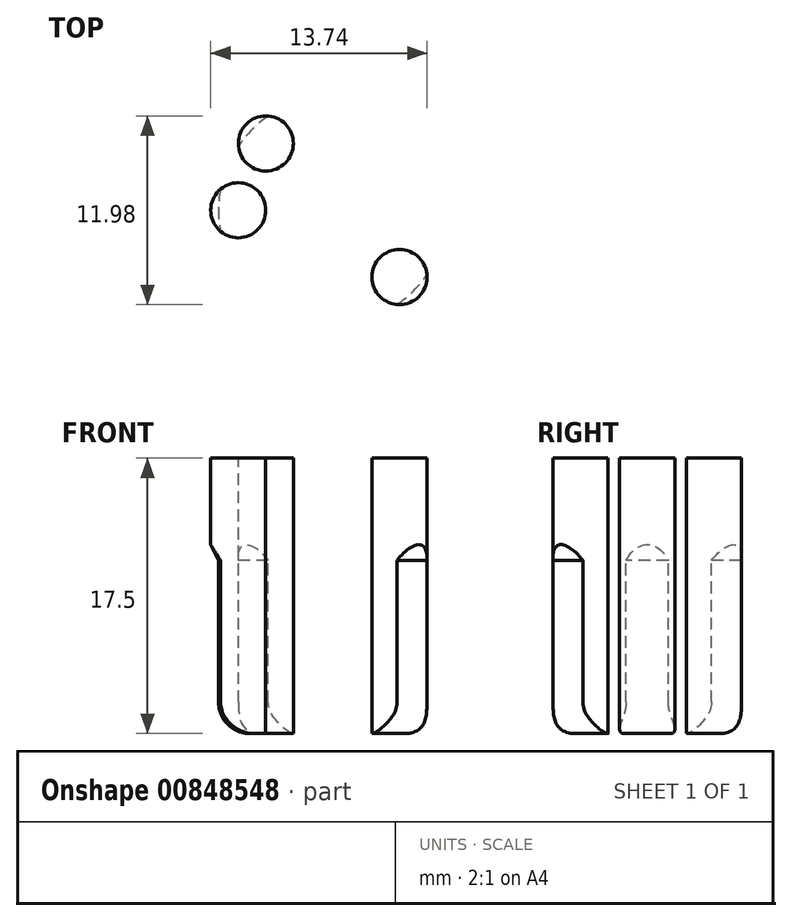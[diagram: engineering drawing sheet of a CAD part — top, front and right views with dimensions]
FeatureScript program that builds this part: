
annotation { "Feature Type Name" : "Feature", "Feature Type Description" : "" }
export const myFeature = defineFeature(function(context is Context, id is Id, definition is map)
    precondition{}
    {
        {
            var Q0;
            Q0=qCreatedBy(makeId("Top.planeOp"),FACE);
            var sketch = newSketch(context, id + "F0", { "sketchPlane" : qUnion([Q0])});
            skCircle(sketch, "E0", {"center": v(0, 0) * mm, "radius": 7.25 * mm});
            skSolve(sketch);
        }
        {
            var Q0;
            Q0 = qSketchRegion(id + "F0", true);
            extrude(context, id + "F1", {"entities" : qUnion([Q0]), "oppositeDirection" : true, "depth" : 10.5 * mm, "offsetDistance" : 25 * mm});
        }
        {
            var Q0;
            Q0=qCreatedBy(makeId("Top.planeOp"),FACE);
            var sketch = newSketch(context, id + "F2", { "sketchPlane" : qUnion([Q0])});
            skCircle(sketch, "E1", {"center": v(0, 0) * mm, "radius": 10 * mm});
            skSolve(sketch);
        }
        {
            var Q0;
            Q0 = qSketchRegion(id + "F2", true);
            extrude(context, id + "F3", {"entities" : qUnion([Q0]), "operationType" : NewBodyOperationType.ADD, "depth" : 7 * mm, "offsetDistance" : 25 * mm});
        }
        {
            var Q0;
            Q0=makeQuery(id+"F3.opExtrude","CAP_EDGE",EDGE,{"disambiguationData":[OSD([sQuery(id+"F2.wireOp",EDGE,"E1")])],"isStart":true});
            chamfer(context, id + "F4", {"entities" : qUnion([Q0]), "chamferType" : ChamferType.TWO_OFFSETS, "width1" : 6 * mm, "oppositeDirection" : false, "width2" : 3 * mm, "tangentPropagation" : true});
        }
        {
            var Q0;
            Q0=makeQuery(id+"F3.opExtrude","CAP_FACE",FACE,{"disambiguationData":[OSD([sQuery(id+"F2.wireOp",EDGE,"E1")])],"isStart":false});
            var sketch = newSketch(context, id + "F5", { "sketchPlane" : qUnion([Q0])});
            skCircle(sketch, "E2", {"center": v(0, 0) * mm, "radius": 2.75 * mm});
            skCircle(sketch, "E3", {"center": v(0, 6) * mm, "radius": 1.75 * mm});
            skLineSegment(sketch, "E4", {"start": v(0, 0) * mm, "end": v(7.93, 7.93) * mm, "construction": true});
            skCircle(sketch, "E5", {"center": v(4.24, 4.24) * mm, "radius": 1.75 * mm});
            skCircle(sketch, "E6.1.0", {"center": v(6, 0) * mm, "radius": 1.75 * mm});
            skCircle(sketch, "E6.2.0", {"center": v(0, -6) * mm, "radius": 1.75 * mm});
            skLineSegment(sketch, "E6.anchor1", {"start": v(0, 0) * mm, "end": v(0, 6) * mm, "construction": true});
            skLineSegment(sketch, "E6.anchor2", {"start": v(0, 0) * mm, "end": v(0, -6) * mm, "construction": true});
            skCircle(sketch, "E7.MirrorC", {"center": v(4.24, -4.24) * mm, "radius": 1.75 * mm});
            skCircle(sketch, "E8.MirrorC", {"center": v(-4.24, 4.24) * mm, "radius": 1.75 * mm});
            skCircle(sketch, "E9.MirrorC", {"center": v(-6, 0) * mm, "radius": 1.75 * mm});
            skCircle(sketch, "E10.MirrorC", {"center": v(-4.24, -4.24) * mm, "radius": 1.75 * mm});
            skSolve(sketch);
        }
        {
            var Q0;
            Q0=makeQuery(id+"F5.imprint","IMPRINT",FACE,{"disambiguationData":[TD([[makeQuery(id+"F5.imprint","IMPRINT",EDGE,{"derivedFrom":sQuery(id+"F5.wireOp",EDGE,"E2")}),1.0]])]});
            extrude(context, id + "F6", {"entities" : qUnion([Q0]), "operationType" : NewBodyOperationType.REMOVE, "oppositeDirection" : true, "depth" : 25 * mm, "offsetDistance" : 25 * mm});
        }
        {
            var Q0;
            Q0=makeQuery(id+"F5.imprint","IMPRINT",FACE,{"disambiguationData":[TD([[makeQuery(id+"F5.imprint","IMPRINT",EDGE,{"derivedFrom":sQuery(id+"F5.wireOp",EDGE,"E5")}),1.0]])]});
            var Q1;
            Q1=makeQuery(id+"F5.imprint","IMPRINT",FACE,{"disambiguationData":[TD([[makeQuery(id+"F5.imprint","IMPRINT",EDGE,{"derivedFrom":sQuery(id+"F5.wireOp",EDGE,"E3")}),1.0]])]});
            var Q2;
            Q2=makeQuery(id+"F5.imprint","IMPRINT",FACE,{"disambiguationData":[TD([[makeQuery(id+"F5.imprint","IMPRINT",EDGE,{"derivedFrom":sQuery(id+"F5.wireOp",EDGE,"E8.MirrorC")}),-1.0]])]});
            var Q3;
            Q3=makeQuery(id+"F5.imprint","IMPRINT",FACE,{"disambiguationData":[TD([[makeQuery(id+"F5.imprint","IMPRINT",EDGE,{"derivedFrom":sQuery(id+"F5.wireOp",EDGE,"E9.MirrorC")}),-1.0]])]});
            var Q4;
            Q4=makeQuery(id+"F5.imprint","IMPRINT",FACE,{"disambiguationData":[TD([[makeQuery(id+"F5.imprint","IMPRINT",EDGE,{"derivedFrom":sQuery(id+"F5.wireOp",EDGE,"E10.MirrorC")}),1.0]])]});
            var Q5;
            Q5=makeQuery(id+"F5.imprint","IMPRINT",FACE,{"disambiguationData":[TD([[makeQuery(id+"F5.imprint","IMPRINT",EDGE,{"derivedFrom":sQuery(id+"F5.wireOp",EDGE,"E6.1.0")}),1.0]])]});
            var Q6;
            Q6=makeQuery(id+"F5.imprint","IMPRINT",FACE,{"disambiguationData":[TD([[makeQuery(id+"F5.imprint","IMPRINT",EDGE,{"derivedFrom":sQuery(id+"F5.wireOp",EDGE,"E6.2.0")}),1.0]])]});
            var Q7;
            Q7=makeQuery(id+"F5.imprint","IMPRINT",FACE,{"disambiguationData":[TD([[makeQuery(id+"F5.imprint","IMPRINT",EDGE,{"derivedFrom":sQuery(id+"F5.wireOp",EDGE,"E7.MirrorC")}),-1.0]])]});
            extrude(context, id + "F7", {"entities" : qUnion([Q0, Q1, Q2, Q3, Q4, Q5, Q6, Q7]), "operationType" : NewBodyOperationType.REMOVE, "oppositeDirection" : true, "depth" : 25 * mm, "offsetDistance" : 25 * mm});
        }
        {
            var Q0;
            {var subQ0=sQuery(id+"F0.wireOp",EDGE,"E0");Q0=makeQuery(id+"F7.boolean.opBoolean","SPLIT",EDGE,{"disambiguationData":[TD([makeQuery(id+"F1.opExtrude","SWEPT_FACE",FACE,{"disambiguationData":[OSD([subQ0])]}),makeQuery(id+"F1.opExtrude","CAP_FACE",FACE,{"disambiguationData":[OSD([subQ0])],"isStart":false}),makeQuery(id+"F7.opExtrude","SWEPT_FACE",FACE,{"disambiguationData":[OSD([sQuery(id+"F5.wireOp",EDGE,"E3")])]}),makeQuery(id+"F7.opExtrude","SWEPT_FACE",FACE,{"disambiguationData":[OSD([sQuery(id+"F5.wireOp",EDGE,"E5")])]})])],"derivedFrom":makeQuery(id+"F1.opExtrude","CAP_EDGE",EDGE,{"disambiguationData":[OSD([subQ0])],"isStart":false})});}
            var Q1;
            {var subQ0=sQuery(id+"F0.wireOp",EDGE,"E0");Q1=makeQuery(id+"F7.boolean.opBoolean","SPLIT",EDGE,{"disambiguationData":[TD([makeQuery(id+"F1.opExtrude","SWEPT_FACE",FACE,{"disambiguationData":[OSD([subQ0])]}),makeQuery(id+"F1.opExtrude","CAP_FACE",FACE,{"disambiguationData":[OSD([subQ0])],"isStart":false}),makeQuery(id+"F7.opExtrude","SWEPT_FACE",FACE,{"disambiguationData":[OSD([sQuery(id+"F5.wireOp",EDGE,"E5")])]}),makeQuery(id+"F7.opExtrude","SWEPT_FACE",FACE,{"disambiguationData":[OSD([sQuery(id+"F5.wireOp",EDGE,"E6.1.0")])]})])],"derivedFrom":makeQuery(id+"F1.opExtrude","CAP_EDGE",EDGE,{"disambiguationData":[OSD([subQ0])],"isStart":false})});}
            var Q2;
            {var subQ0=sQuery(id+"F0.wireOp",EDGE,"E0");Q2=makeQuery(id+"F7.boolean.opBoolean","SPLIT",EDGE,{"disambiguationData":[TD([makeQuery(id+"F1.opExtrude","SWEPT_FACE",FACE,{"disambiguationData":[OSD([subQ0])]}),makeQuery(id+"F1.opExtrude","CAP_FACE",FACE,{"disambiguationData":[OSD([subQ0])],"isStart":false}),makeQuery(id+"F7.opExtrude","SWEPT_FACE",FACE,{"disambiguationData":[OSD([sQuery(id+"F5.wireOp",EDGE,"E3")])]}),makeQuery(id+"F7.opExtrude","SWEPT_FACE",FACE,{"disambiguationData":[OSD([sQuery(id+"F5.wireOp",EDGE,"E8.MirrorC")])]})])],"derivedFrom":makeQuery(id+"F1.opExtrude","CAP_EDGE",EDGE,{"disambiguationData":[OSD([subQ0])],"isStart":false})});}
            var Q3;
            {var subQ0=sQuery(id+"F0.wireOp",EDGE,"E0");Q3=makeQuery(id+"F7.boolean.opBoolean","SPLIT",EDGE,{"disambiguationData":[TD([makeQuery(id+"F1.opExtrude","SWEPT_FACE",FACE,{"disambiguationData":[OSD([subQ0])]}),makeQuery(id+"F1.opExtrude","CAP_FACE",FACE,{"disambiguationData":[OSD([subQ0])],"isStart":false}),makeQuery(id+"F7.opExtrude","SWEPT_FACE",FACE,{"disambiguationData":[OSD([sQuery(id+"F5.wireOp",EDGE,"E8.MirrorC")])]}),makeQuery(id+"F7.opExtrude","SWEPT_FACE",FACE,{"disambiguationData":[OSD([sQuery(id+"F5.wireOp",EDGE,"E9.MirrorC")])]})])],"derivedFrom":makeQuery(id+"F1.opExtrude","CAP_EDGE",EDGE,{"disambiguationData":[OSD([subQ0])],"isStart":false})});}
            var Q4;
            {var subQ0=sQuery(id+"F0.wireOp",EDGE,"E0");Q4=makeQuery(id+"F7.boolean.opBoolean","SPLIT",EDGE,{"disambiguationData":[TD([makeQuery(id+"F1.opExtrude","SWEPT_FACE",FACE,{"disambiguationData":[OSD([subQ0])]}),makeQuery(id+"F1.opExtrude","CAP_FACE",FACE,{"disambiguationData":[OSD([subQ0])],"isStart":false}),makeQuery(id+"F7.opExtrude","SWEPT_FACE",FACE,{"disambiguationData":[OSD([sQuery(id+"F5.wireOp",EDGE,"E9.MirrorC")])]}),makeQuery(id+"F7.opExtrude","SWEPT_FACE",FACE,{"disambiguationData":[OSD([sQuery(id+"F5.wireOp",EDGE,"E10.MirrorC")])]})])],"derivedFrom":makeQuery(id+"F1.opExtrude","CAP_EDGE",EDGE,{"disambiguationData":[OSD([subQ0])],"isStart":false})});}
            var Q5;
            {var subQ0=sQuery(id+"F0.wireOp",EDGE,"E0");Q5=makeQuery(id+"F7.boolean.opBoolean","SPLIT",EDGE,{"disambiguationData":[TD([makeQuery(id+"F1.opExtrude","SWEPT_FACE",FACE,{"disambiguationData":[OSD([subQ0])]}),makeQuery(id+"F1.opExtrude","CAP_FACE",FACE,{"disambiguationData":[OSD([subQ0])],"isStart":false}),makeQuery(id+"F7.opExtrude","SWEPT_FACE",FACE,{"disambiguationData":[OSD([sQuery(id+"F5.wireOp",EDGE,"E6.2.0")])]}),makeQuery(id+"F7.opExtrude","SWEPT_FACE",FACE,{"disambiguationData":[OSD([sQuery(id+"F5.wireOp",EDGE,"E10.MirrorC")])]})])],"derivedFrom":makeQuery(id+"F1.opExtrude","CAP_EDGE",EDGE,{"disambiguationData":[OSD([subQ0])],"isStart":false})});}
            var Q6;
            {var subQ0=sQuery(id+"F0.wireOp",EDGE,"E0");Q6=makeQuery(id+"F7.boolean.opBoolean","SPLIT",EDGE,{"disambiguationData":[TD([makeQuery(id+"F1.opExtrude","SWEPT_FACE",FACE,{"disambiguationData":[OSD([subQ0])]}),makeQuery(id+"F1.opExtrude","CAP_FACE",FACE,{"disambiguationData":[OSD([subQ0])],"isStart":false}),makeQuery(id+"F7.opExtrude","SWEPT_FACE",FACE,{"disambiguationData":[OSD([sQuery(id+"F5.wireOp",EDGE,"E6.2.0")])]}),makeQuery(id+"F7.opExtrude","SWEPT_FACE",FACE,{"disambiguationData":[OSD([sQuery(id+"F5.wireOp",EDGE,"E7.MirrorC")])]})])],"derivedFrom":makeQuery(id+"F1.opExtrude","CAP_EDGE",EDGE,{"disambiguationData":[OSD([subQ0])],"isStart":false})});}
            var Q7;
            {var subQ0=sQuery(id+"F0.wireOp",EDGE,"E0");Q7=makeQuery(id+"F7.boolean.opBoolean","SPLIT",EDGE,{"disambiguationData":[TD([makeQuery(id+"F1.opExtrude","SWEPT_FACE",FACE,{"disambiguationData":[OSD([subQ0])]}),makeQuery(id+"F1.opExtrude","CAP_FACE",FACE,{"disambiguationData":[OSD([subQ0])],"isStart":false}),makeQuery(id+"F7.opExtrude","SWEPT_FACE",FACE,{"disambiguationData":[OSD([sQuery(id+"F5.wireOp",EDGE,"E6.1.0")])]}),makeQuery(id+"F7.opExtrude","SWEPT_FACE",FACE,{"disambiguationData":[OSD([sQuery(id+"F5.wireOp",EDGE,"E7.MirrorC")])]})])],"derivedFrom":makeQuery(id+"F1.opExtrude","CAP_EDGE",EDGE,{"disambiguationData":[OSD([subQ0])],"isStart":false})});}
            var Q8;
            Q8=makeQuery(id+"F6.boolean.opBoolean","INTERSECT",EDGE,{"derivedFrom":[makeQuery(id+"F1.opExtrude","CAP_FACE",FACE,{"disambiguationData":[OSD([sQuery(id+"F0.wireOp",EDGE,"E0")])],"isStart":false}),makeQuery(id+"F6.opExtrude","SWEPT_FACE",FACE,{"disambiguationData":[OSD([sQuery(id+"F5.wireOp",EDGE,"E2")])]})]});
            var Q9;
            {var subQ0=sQuery(id+"F2.wireOp",EDGE,"E1");Q9=makeQuery(id+"F4.opChamfer","BLEND_EDGE",EDGE,{"blendedFrom":[makeQuery(id+"F3.opExtrude","CAP_EDGE",EDGE,{"disambiguationData":[OSD([subQ0])],"isStart":true}),makeQuery(id+"F3.opExtrude","SWEPT_FACE",FACE,{"disambiguationData":[OSD([subQ0])]})],"blendedInto":[makeQuery(id+"F3.opExtrude","SWEPT_FACE",FACE,{"disambiguationData":[OSD([subQ0])]})]});}
            fillet(context, id + "F8", {"entities" : qUnion([Q0, Q1, Q2, Q3, Q4, Q5, Q6, Q7, Q8, Q9]), "radius" : 2 * mm, "tangentPropagation" : true, "allowEdgeOverflow" : false});
        }
    });
